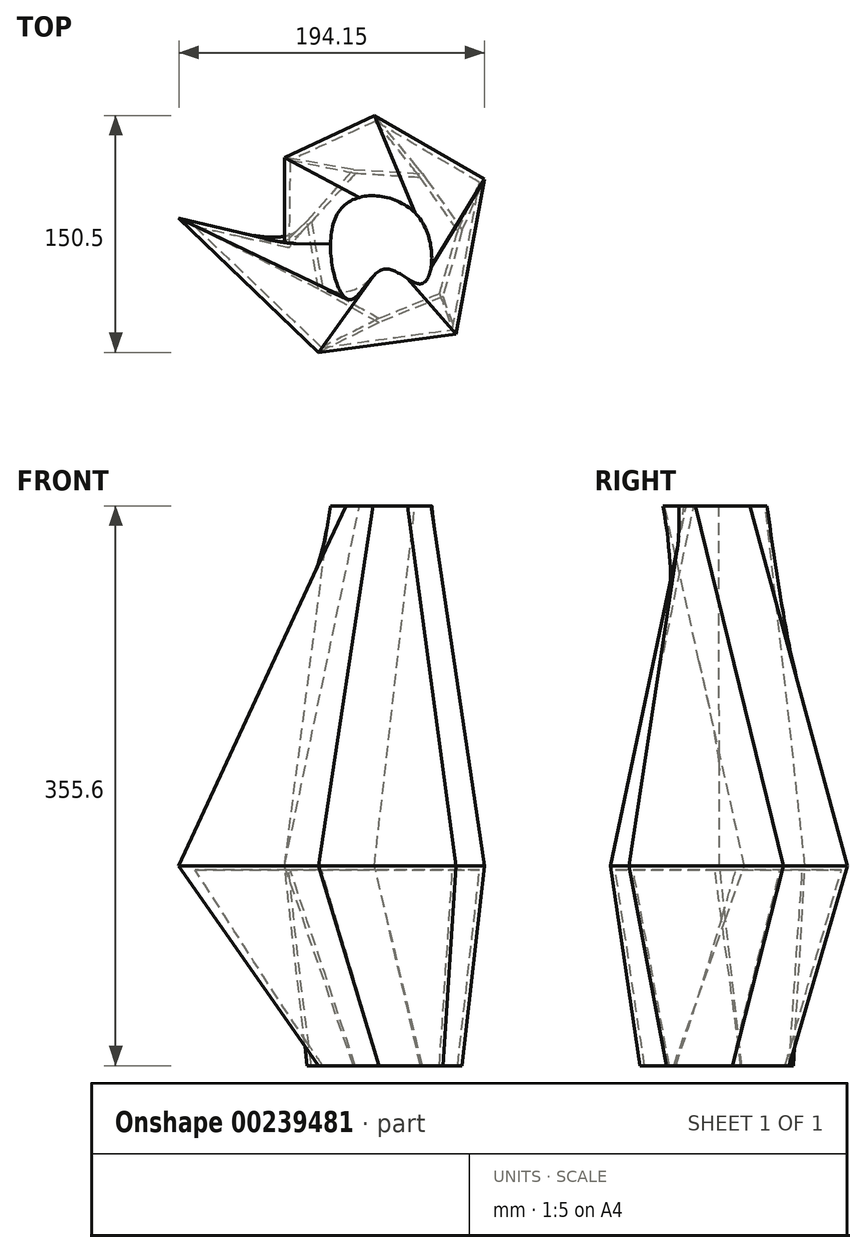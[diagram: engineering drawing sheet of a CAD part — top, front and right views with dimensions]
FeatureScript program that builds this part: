
annotation { "Feature Type Name" : "Feature", "Feature Type Description" : "" }
export const myFeature = defineFeature(function(context is Context, id is Id, definition is map)
    precondition{}
    {
        {
            var Q0;
            Q0=qCreatedBy(makeId("Top.planeOp"),FACE);
            cPlane(context, id + "F0", {"entities" : qUnion([Q0]), "cplaneType" : CPlaneType.OFFSET, "offset" : 127 * mm, "width" : 152.4 * mm, "height" : 152.4 * mm});
        }
        {
            var Q0;
            Q0=qCreatedBy(makeId("Top.planeOp"),FACE);
            var sketch = newSketch(context, id + "F1", { "sketchPlane" : qUnion([Q0])});
            skCircle(sketch, "E0.cCircle", {"center": v(0, 0) * mm, "radius": 45.6 * mm, "construction": true});
            skLineSegment(sketch, "E0.0", {"start": v(-48.59, 14.2) * mm, "end": v(-19.18, 46.84) * mm});
            skLineSegment(sketch, "E0.1", {"start": v(-19.18, 46.84) * mm, "end": v(24.66, 44.2) * mm});
            skLineSegment(sketch, "E0.2", {"start": v(24.66, 44.2) * mm, "end": v(49.94, 8.28) * mm});
            skLineSegment(sketch, "E0.3", {"start": v(49.94, 8.28) * mm, "end": v(37.6, -33.88) * mm});
            skLineSegment(sketch, "E0.4", {"start": v(37.6, -33.88) * mm, "end": v(-3.04, -50.53) * mm});
            skLineSegment(sketch, "E0.5", {"start": v(-3.04, -50.53) * mm, "end": v(-41.4, -29.13) * mm});
            skLineSegment(sketch, "E0.6", {"start": v(-41.4, -29.13) * mm, "end": v(-48.59, 14.2) * mm});
            skPoint(sketch, "E0.0.midPoint", {"position": v(-33.88, 30.53) * mm});
            skSolve(sketch);
        }
        {
            var Q0;
            Q0=qCreatedBy(id+"F0.planeOp",FACE);
            var sketch = newSketch(context, id + "F2", { "sketchPlane" : qUnion([Q0])});
            skLineSegment(sketch, "E1", {"start": v(-62.89, 0) * mm, "end": v(-62.89, 54.34) * mm});
            skLineSegment(sketch, "E2", {"start": v(-62.89, 54.34) * mm, "end": v(-5.8, 81.2) * mm});
            skLineSegment(sketch, "E3", {"start": v(-5.8, 81.2) * mm, "end": v(64.1, 40.6) * mm});
            skLineSegment(sketch, "E4", {"start": v(64.1, 40.6) * mm, "end": v(46.1, -57.7) * mm});
            skLineSegment(sketch, "E5", {"start": v(46.1, -57.7) * mm, "end": v(-41.21, -69.3) * mm});
            skLineSegment(sketch, "E6", {"start": v(-41.21, -69.3) * mm, "end": v(-130.04, 15.87) * mm});
            skLineSegment(sketch, "E7", {"start": v(-130.04, 15.87) * mm, "end": v(-62.89, 0) * mm});
            skSolve(sketch);
        }
        {
            var Q0;
            Q0 = qSketchRegion(id + "F1", true);
            var Q1;
            Q1 = qSketchRegion(id + "F2", true);
            loft(context, id + "F3", {"sheetProfilesArray" : [{ "sheetProfileEntities" : qUnion([Q0]) }, { "sheetProfileEntities" : qUnion([Q1]) }]});
        }
        {
            var Q0;
            Q0=makeQuery(id+"F3.opLoft","CAP_FACE",FACE,{"disambiguationData":[OSD([makeQuery(id+"F1.imprint","IMPRINT",FACE,{"disambiguationData":[TD([[makeQuery(id+"F1.imprint","IMPRINT",EDGE,{"derivedFrom":sQuery(id+"F1.wireOp",EDGE,"E0.0")}),-1.0]])]})])],"isStart":true});
            shell(context, id + "F4", {"entities" : qUnion([Q0]), "thickness" : 2.54 * mm});
        }
        {
            var Q0;
            Q0=qCreatedBy(id+"F0.planeOp",FACE);
            cPlane(context, id + "F5", {"entities" : qUnion([Q0]), "cplaneType" : CPlaneType.OFFSET, "offset" : 228.6 * mm, "width" : 152.4 * mm, "height" : 152.4 * mm});
        }
        {
            var Q0;
            Q0=qCreatedBy(id+"F5.planeOp",FACE);
            var sketch = newSketch(context, id + "F6", { "sketchPlane" : qUnion([Q0])});
            skFitSpline(sketch, "E8", {"points": [v(-21.8, -35.86) * mm, v(-28.6, 19.87) * mm, v(22.78, 16) * mm, v(24.23, -25.68) * mm, v(0, -16.48) * mm, v(-21.8, -35.86) * mm]});
            skSolve(sketch);
        }
        {
            var Q1;
            Q1=makeQuery(id+"F3.opLoft","CAP_FACE",FACE,{"disambiguationData":[OSD([makeQuery(id+"F2.imprint","IMPRINT",FACE,{"disambiguationData":[TD([[makeQuery(id+"F2.imprint","IMPRINT",EDGE,{"derivedFrom":sQuery(id+"F2.wireOp",EDGE,"E1")}),-1.0]])]})])],"isStart":true});
            var Q2;
            Q2=makeQuery(id+"F6.imprint","IMPRINT",FACE,{"disambiguationData":[TD([[makeQuery(id+"F6.imprint","IMPRINT",EDGE,{"derivedFrom":sQuery(id+"F6.wireOp",EDGE,"E8")}),-1.0]])]});
            loft(context, id + "F7", {"operationType" : NewBodyOperationType.ADD, "sheetProfilesArray" : [{ "sheetProfileEntities" : qUnion([Q1]) }, { "sheetProfileEntities" : qUnion([Q2]) }]});
        }
    });
